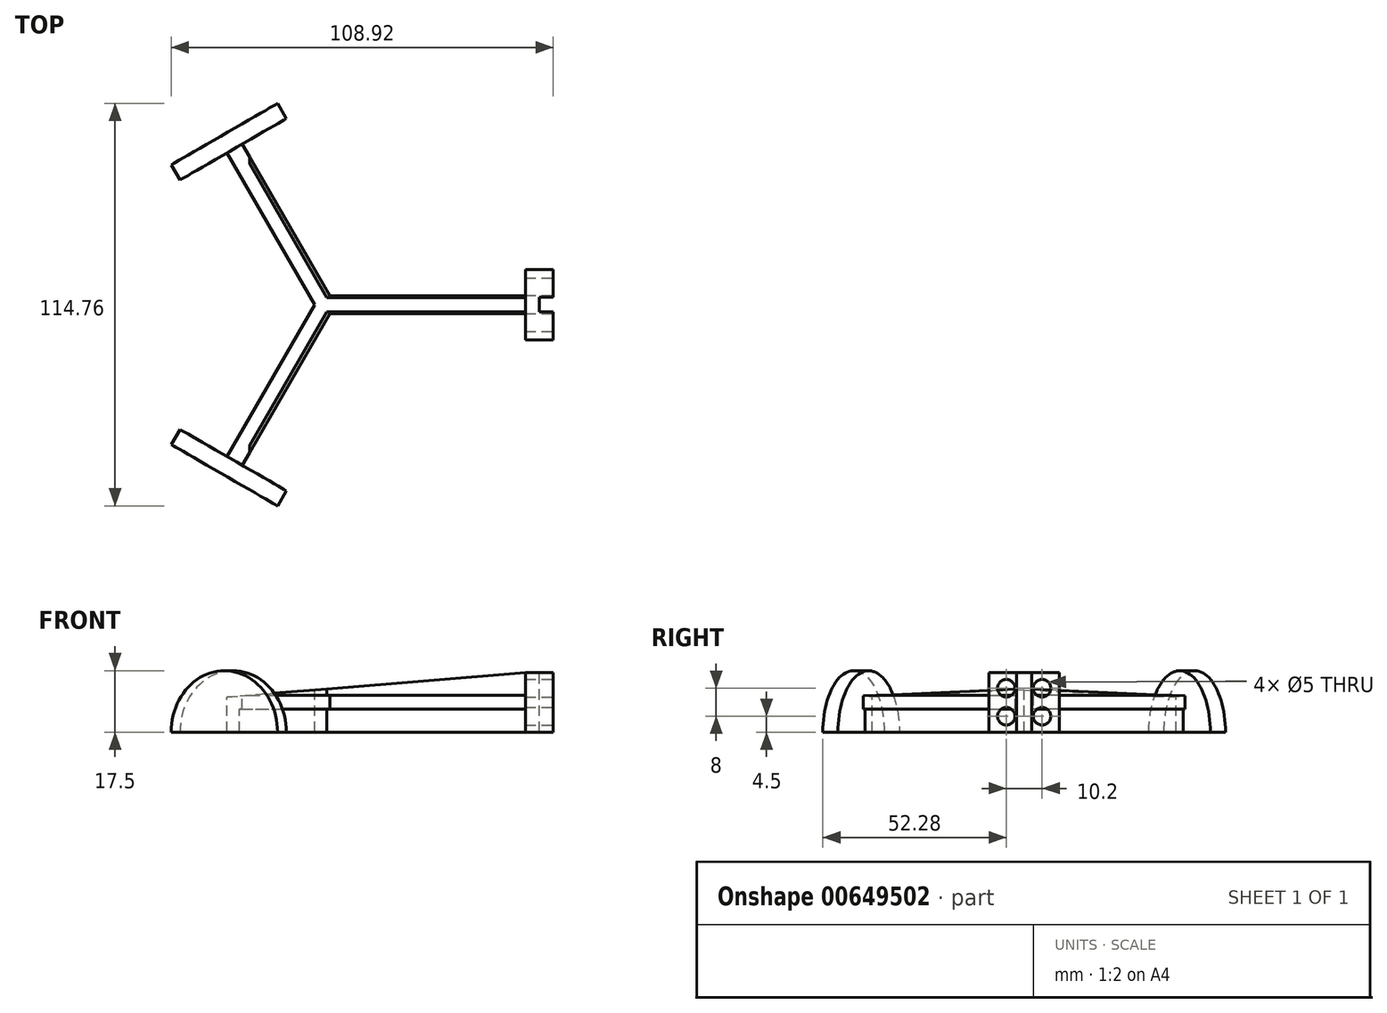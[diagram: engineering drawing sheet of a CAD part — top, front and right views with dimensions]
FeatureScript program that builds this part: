
annotation { "Feature Type Name" : "Feature", "Feature Type Description" : "" }
export const myFeature = defineFeature(function(context is Context, id is Id, definition is map)
    precondition{}
    {
        {
            var Q0;
            Q0=qCreatedBy(makeId("Right.planeOp"),FACE);
            var sketch = newSketch(context, id + "F0", { "sketchPlane" : qUnion([Q0])});
            skLineSegment(sketch, "E0.bottom", {"start": v(-10, 8.5) * mm, "end": v(10, 8.5) * mm});
            skLineSegment(sketch, "E0.top", {"start": v(-10, -8.5) * mm, "end": v(10, -8.5) * mm});
            skLineSegment(sketch, "E0.left", {"start": v(-10, 8.5) * mm, "end": v(-10, -8.5) * mm});
            skLineSegment(sketch, "E0.right", {"start": v(10, 8.5) * mm, "end": v(10, -8.5) * mm});
            skSolve(sketch);
        }
        {
            var Q0;
            Q0 = qSketchRegion(id + "F0", true);
            var Q1;
            Q1 = qSketchRegion(id + "F2", true);
            extrude(context, id + "F1", {"entities" : qUnion([Q0, Q1]), "depth" : 8 * mm, "offsetDistance" : 25 * mm});
        }
        {
            var Q0;
            Q0=makeQuery(id+"F1.opExtrude","SWEPT_FACE",FACE,{"disambiguationData":[OSD([sQuery(id+"F0.wireOp",EDGE,"E0.bottom")])]});
            var sketch = newSketch(context, id + "F2", { "sketchPlane" : qUnion([Q0])});
            skLineSegment(sketch, "E1", {"start": v(-0.34, 0) * mm, "end": v(8.66, 0) * mm, "construction": true});
            skPoint(sketch, "E1.endSnap0", {"position": v(8, 0) * mm});
            skLineSegment(sketch, "E2", {"start": v(4, -10) * mm, "end": v(4, 7.8) * mm, "construction": true});
            skLineSegment(sketch, "E3.bottom", {"start": v(8, -2.1) * mm, "end": v(4, -2.1) * mm});
            skLineSegment(sketch, "E3.top", {"start": v(8, 2.1) * mm, "end": v(4, 2.1) * mm});
            skLineSegment(sketch, "E3.left", {"start": v(8, -2.1) * mm, "end": v(8, 2.1) * mm});
            skLineSegment(sketch, "E3.right", {"start": v(4, -2.1) * mm, "end": v(4, 2.1) * mm});
            skSolve(sketch);
        }
        {
            var Q0;
            Q0 = qSketchRegion(id + "F2", true);
            extrude(context, id + "F3", {"entities" : qUnion([Q0]), "operationType" : NewBodyOperationType.REMOVE, "endBound" : BoundingType.THROUGH_ALL, "oppositeDirection" : true, "depth" : 25 * mm, "offsetDistance" : 25 * mm});
        }
        {
            var Q0;
            {var subQ0=sQuery(id+"F0.wireOp",EDGE,"E0.bottom");var subQ1=sQuery(id+"F0.wireOp",EDGE,"E0.top");var subQ2=sQuery(id+"F0.wireOp",EDGE,"E0.left");Q0=makeQuery(id+"F3.boolean.opBoolean","SPLIT",FACE,{"disambiguationData":[TD([makeQuery(id+"F1.opExtrude","SWEPT_FACE",FACE,{"disambiguationData":[OSD([subQ2])]})])],"derivedFrom":makeQuery(id+"F1.opExtrude","CAP_FACE",FACE,{"disambiguationData":[OSD([subQ0,subQ1,subQ2,sQuery(id+"F0.wireOp",EDGE,"E0.right")])],"isStart":false})});}
            var sketch = newSketch(context, id + "F4", { "sketchPlane" : qUnion([Q0])});
            skLineSegment(sketch, "E4", {"start": v(0, 0) * mm, "end": v(-10.22, 0) * mm});
            skLineSegment(sketch, "E5", {"start": v(0.75, 4) * mm, "end": v(-10.14, 4) * mm, "construction": true});
            skLineSegment(sketch, "E6", {"start": v(0.4, -4) * mm, "end": v(-10.72, -4) * mm, "construction": true});
            skLineSegment(sketch, "E7", {"start": v(-10, 7.92) * mm, "end": v(-10, -5.77) * mm, "construction": true});
            skLineSegment(sketch, "E8", {"start": v(-2.1, 7.55) * mm, "end": v(-2.1, -5.11) * mm, "construction": true});
            skCircle(sketch, "E9", {"center": v(-5.1, 4) * mm, "radius": 2.5 * mm});
            skLineSegment(sketch, "E10", {"start": v(0, 0) * mm, "end": v(0, 8.72) * mm, "construction": true});
            skCircle(sketch, "E11.MirrorC", {"center": v(5.1, 4) * mm, "radius": 2.5 * mm});
            skCircle(sketch, "E12.MirrorC", {"center": v(-5.1, -4) * mm, "radius": 2.5 * mm});
            skCircle(sketch, "E13.MirrorC", {"center": v(5.1, -4) * mm, "radius": 2.5 * mm});
            skSolve(sketch);
        }
        {
            var Q0;
            Q0 = qSketchRegion(id + "F4", true);
            extrude(context, id + "F5", {"entities" : qUnion([Q0]), "operationType" : NewBodyOperationType.REMOVE, "endBound" : BoundingType.THROUGH_ALL, "oppositeDirection" : true, "depth" : 25 * mm, "offsetDistance" : 25 * mm});
        }
        {
            var Q0;
            Q0=qCreatedBy(makeId("Right.planeOp"),FACE);
            var sketch = newSketch(context, id + "F6", { "sketchPlane" : qUnion([Q0])});
            skLineSegment(sketch, "E14", {"start": v(9.15, -5.34) * mm, "end": v(9.15, 7.7) * mm, "construction": true});
            skLineSegment(sketch, "E15", {"start": v(-9.18, 6.7) * mm, "end": v(-9.18, -5.07) * mm, "construction": true});
            skLineSegment(sketch, "E16", {"start": v(0, 0) * mm, "end": v(0, 8.8) * mm, "construction": true});
            skLineSegment(sketch, "E17", {"start": v(0, 8.8) * mm, "end": v(0, 0) * mm, "construction": true});
            skLineSegment(sketch, "E18", {"start": v(0, 0) * mm, "end": v(10.35, 0) * mm, "construction": true});
            skLineSegment(sketch, "E19", {"start": v(10.35, 0) * mm, "end": v(-10.2, 0) * mm, "construction": true});
            skLineSegment(sketch, "E20", {"start": v(-10.2, 0) * mm, "end": v(0, 0) * mm, "construction": true});
            skLineSegment(sketch, "E21", {"start": v(0, -8.1) * mm, "end": v(0, -6.16) * mm, "construction": true});
            skLineSegment(sketch, "E22", {"start": v(0, -6.16) * mm, "end": v(0, 1.53) * mm, "construction": true});
            skLineSegment(sketch, "E23.bottom", {"start": v(2, 8.5) * mm, "end": v(-2, 8.5) * mm});
            skLineSegment(sketch, "E23.top", {"start": v(2, -8.5) * mm, "end": v(-2, -8.5) * mm});
            skLineSegment(sketch, "E23.left", {"start": v(2, 8.5) * mm, "end": v(2, -8.5) * mm});
            skLineSegment(sketch, "E23.right", {"start": v(-2, 8.5) * mm, "end": v(-2, -8.5) * mm});
            skLineSegment(sketch, "E24.bottom", {"start": v(2.5, 2) * mm, "end": v(-2.5, 2) * mm});
            skLineSegment(sketch, "E24.top", {"start": v(2.5, -2) * mm, "end": v(-2.5, -2) * mm});
            skLineSegment(sketch, "E24.left", {"start": v(2.5, 2) * mm, "end": v(2.5, -2) * mm});
            skLineSegment(sketch, "E24.right", {"start": v(-2.5, 2) * mm, "end": v(-2.5, -2) * mm});
            skSolve(sketch);
        }
        {
            var Q0;
            Q0 = qSketchRegion(id + "F6", true);
            extrude(context, id + "F7", {"entities" : qUnion([Q0]), "operationType" : NewBodyOperationType.ADD, "oppositeDirection" : true, "depth" : 60 * mm, "offsetDistance" : 25 * mm});
        }
        {
            var Q0;
            Q0=makeQuery(id+"F7.boolean.opBoolean","MERGE",FACE,{"derivedFrom":[makeQuery(id+"F1.opExtrude","SWEPT_FACE",FACE,{"disambiguationData":[OSD([sQuery(id+"F0.wireOp",EDGE,"E0.bottom")])]}),makeQuery(id+"F7.opExtrude","SWEPT_FACE",FACE,{"disambiguationData":[OSD([sQuery(id+"F6.wireOp",EDGE,"E23.bottom")])]})]});
            var sketch = newSketch(context, id + "F8", { "sketchPlane" : qUnion([Q0])});
            skLineSegment(sketch, "E25", {"start": v(-60, 0) * mm, "end": v(-38.43, 0) * mm, "construction": true});
            skLineSegment(sketch, "E26", {"start": v(-55.67, -2.5) * mm, "end": v(-60, 0) * mm});
            skLineSegment(sketch, "E27", {"start": v(-60, -2.5) * mm, "end": v(-55.67, -2.5) * mm});
            skLineSegment(sketch, "E28", {"start": v(-60, 0) * mm, "end": v(-60, -2.5) * mm});
            skLineSegment(sketch, "E29.MirrorCS", {"start": v(-55.67, 2.5) * mm, "end": v(-60, 0) * mm});
            skLineSegment(sketch, "E30.MirrorCS", {"start": v(-60, 2.5) * mm, "end": v(-55.67, 2.5) * mm});
            skLineSegment(sketch, "E31.MirrorCS", {"start": v(-60, 0) * mm, "end": v(-60, 2.5) * mm});
            skSolve(sketch);
        }
        {
            var Q0;
            Q0 = qSketchRegion(id + "F8", true);
            extrude(context, id + "F9", {"entities" : qUnion([Q0]), "operationType" : NewBodyOperationType.REMOVE, "endBound" : BoundingType.THROUGH_ALL, "oppositeDirection" : true, "depth" : 25 * mm, "offsetDistance" : 25 * mm});
        }
        {
            var Q0;
            Q0=makeQuery(id+"F9.boolean.opBoolean","COPY",FACE,{"derivedFrom":makeQuery(id+"F9.opExtrude","SWEPT_FACE",FACE,{"disambiguationData":[OSD([sQuery(id+"F8.wireOp",EDGE,"E26")])]})});
            extrude(context, id + "F10", {"entities" : qUnion([Q0]), "operationType" : NewBodyOperationType.ADD, "depth" : 50 * mm, "offsetDistance" : 25 * mm});
        }
        {
            var Q0;
            Q0=makeQuery(id+"F9.boolean.opBoolean","COPY",FACE,{"derivedFrom":makeQuery(id+"F9.opExtrude","SWEPT_FACE",FACE,{"disambiguationData":[OSD([sQuery(id+"F8.wireOp",EDGE,"E29.MirrorCS")])]})});
            extrude(context, id + "F11", {"entities" : qUnion([Q0]), "operationType" : NewBodyOperationType.ADD, "depth" : 50 * mm, "offsetDistance" : 25 * mm});
        }
        {
            var Q0;
            {var subQ0=sQuery(id+"F6.wireOp",EDGE,"E23.right");Q0=makeQuery(id+"F7.opExtrude","SWEPT_FACE",FACE,{"disambiguationData":[OSD([subQ0]),TDD([makeQuery(id+"F6.imprint","IMPRINT",EDGE,{"disambiguationData":[TD([[makeQuery(id+"F6.imprint","INTERSECT",VERTEX,{"derivedFrom":[sQuery(id+"F6.wireOp",EDGE,"E23.bottom"),subQ0]}),-1.0]])],"derivedFrom":subQ0})])]});}
            var sketch = newSketch(context, id + "F12", { "sketchPlane" : qUnion([Q0])});
            skLineSegment(sketch, "E32", {"start": v(-56.54, 8.5) * mm, "end": v(0, 8.5) * mm});
            skLineSegment(sketch, "E33", {"start": v(0, 8.5) * mm, "end": v(-90.07, 1.05) * mm, "construction": true});
            skLineSegment(sketch, "E34", {"start": v(-90.07, 1.05) * mm, "end": v(-90.07, 12.65) * mm, "construction": true});
            skLineSegment(sketch, "E35", {"start": v(-90.07, 12.65) * mm, "end": v(0, 8.5) * mm, "construction": true});
            skLineSegment(sketch, "E36", {"start": v(-90.07, 12.65) * mm, "end": v(0, 8.5) * mm});
            skLineSegment(sketch, "E37", {"start": v(-90.07, 1.05) * mm, "end": v(-90.07, 12.65) * mm});
            skLineSegment(sketch, "E38", {"start": v(-90.07, 1.05) * mm, "end": v(0, 8.5) * mm});
            skSolve(sketch);
        }
        {
            var Q0;
            Q0 = qSketchRegion(id + "F12", true);
            extrude(context, id + "F13", {"entities" : qUnion([Q0]), "operationType" : NewBodyOperationType.REMOVE, "endBound" : BoundingType.THROUGH_ALL, "oppositeDirection" : true, "depth" : 100 * mm, "offsetDistance" : 25 * mm});
        }
        {
            var Q0;
            Q0 = qSketchRegion(id + "F12", true);
            extrude(context, id + "F14", {"entities" : qUnion([Q0]), "operationType" : NewBodyOperationType.REMOVE, "endBound" : BoundingType.THROUGH_ALL, "depth" : 25 * mm, "offsetDistance" : 25 * mm});
        }
        {
            var Q0;
            Q0=makeQuery(id+"F10.opExtrude","CAP_FACE",FACE,{"disambiguationData":[OSD([sQuery(id+"F8.wireOp",EDGE,"E26")])],"isStart":false});
            var sketch = newSketch(context, id + "F15", { "sketchPlane" : qUnion([Q0])});
            skLineSegment(sketch, "E39", {"start": v(-49.96, -8.5) * mm, "end": v(-49.96, 9.98) * mm, "construction": true});
            skLineSegment(sketch, "E40", {"start": v(-47.96, -2) * mm, "end": v(-54.65, -2) * mm, "construction": true});
            skCircle(sketch, "E41", {"center": v(-49.96, -8.5) * mm, "radius": 17.5 * mm});
            skSolve(sketch);
        }
        {
            var Q0;
            Q0 = qSketchRegion(id + "F15", true);
            extrude(context, id + "F16", {"entities" : qUnion([Q0]), "operationType" : NewBodyOperationType.ADD, "depth" : 5 * mm, "offsetDistance" : 25 * mm});
        }
        {
            var Q0;
            Q0=makeQuery(id+"F11.opExtrude","CAP_FACE",FACE,{"disambiguationData":[OSD([sQuery(id+"F8.wireOp",EDGE,"E29.MirrorCS")])],"isStart":false});
            var sketch = newSketch(context, id + "F17", { "sketchPlane" : qUnion([Q0])});
            skCircle(sketch, "E42", {"center": v(49.96, -8.5) * mm, "radius": 17.5 * mm});
            skSolve(sketch);
        }
        {
            var Q0;
            Q0 = qSketchRegion(id + "F17", true);
            extrude(context, id + "F18", {"entities" : qUnion([Q0]), "operationType" : NewBodyOperationType.ADD, "depth" : 5 * mm, "offsetDistance" : 25 * mm});
        }
        {
            var Q0;
            {var subQ0=sQuery(id+"F0.wireOp",EDGE,"E0.bottom");var subQ1=sQuery(id+"F0.wireOp",EDGE,"E0.top");var subQ2=sQuery(id+"F0.wireOp",EDGE,"E0.left");Q0=makeQuery(id+"F3.boolean.opBoolean","SPLIT",FACE,{"disambiguationData":[TD([makeQuery(id+"F1.opExtrude","SWEPT_FACE",FACE,{"disambiguationData":[OSD([subQ2])]})])],"derivedFrom":makeQuery(id+"F1.opExtrude","CAP_FACE",FACE,{"disambiguationData":[OSD([subQ0,subQ1,subQ2,sQuery(id+"F0.wireOp",EDGE,"E0.right")])],"isStart":false})});}
            var sketch = newSketch(context, id + "F19", { "sketchPlane" : qUnion([Q0])});
            skLineSegment(sketch, "E43", {"start": v(0, 0) * mm, "end": v(0, -13.9) * mm, "construction": true});
            skLineSegment(sketch, "E44", {"start": v(-3.45, -8.5) * mm, "end": v(7.58, -8.5) * mm, "construction": true});
            skLineSegment(sketch, "E45", {"start": v(0, -8.5) * mm, "end": v(63.88, -8.5) * mm});
            skLineSegment(sketch, "E46", {"start": v(63.88, -8.5) * mm, "end": v(63.88, -28.59) * mm});
            skLineSegment(sketch, "E47", {"start": v(63.88, -28.59) * mm, "end": v(-60.02, -29.48) * mm});
            skLineSegment(sketch, "E48", {"start": v(0, -8.5) * mm, "end": v(-60.12, -8.5) * mm});
            skLineSegment(sketch, "E49", {"start": v(-60.12, -8.5) * mm, "end": v(-60.02, -29.48) * mm});
            skSolve(sketch);
        }
        {
            var Q0;
            Q0 = qSketchRegion(id + "F19", true);
            extrude(context, id + "F20", {"entities" : qUnion([Q0]), "operationType" : NewBodyOperationType.REMOVE, "endBound" : BoundingType.THROUGH_ALL, "oppositeDirection" : true, "depth" : 25 * mm, "offsetDistance" : 25 * mm});
        }
    });
